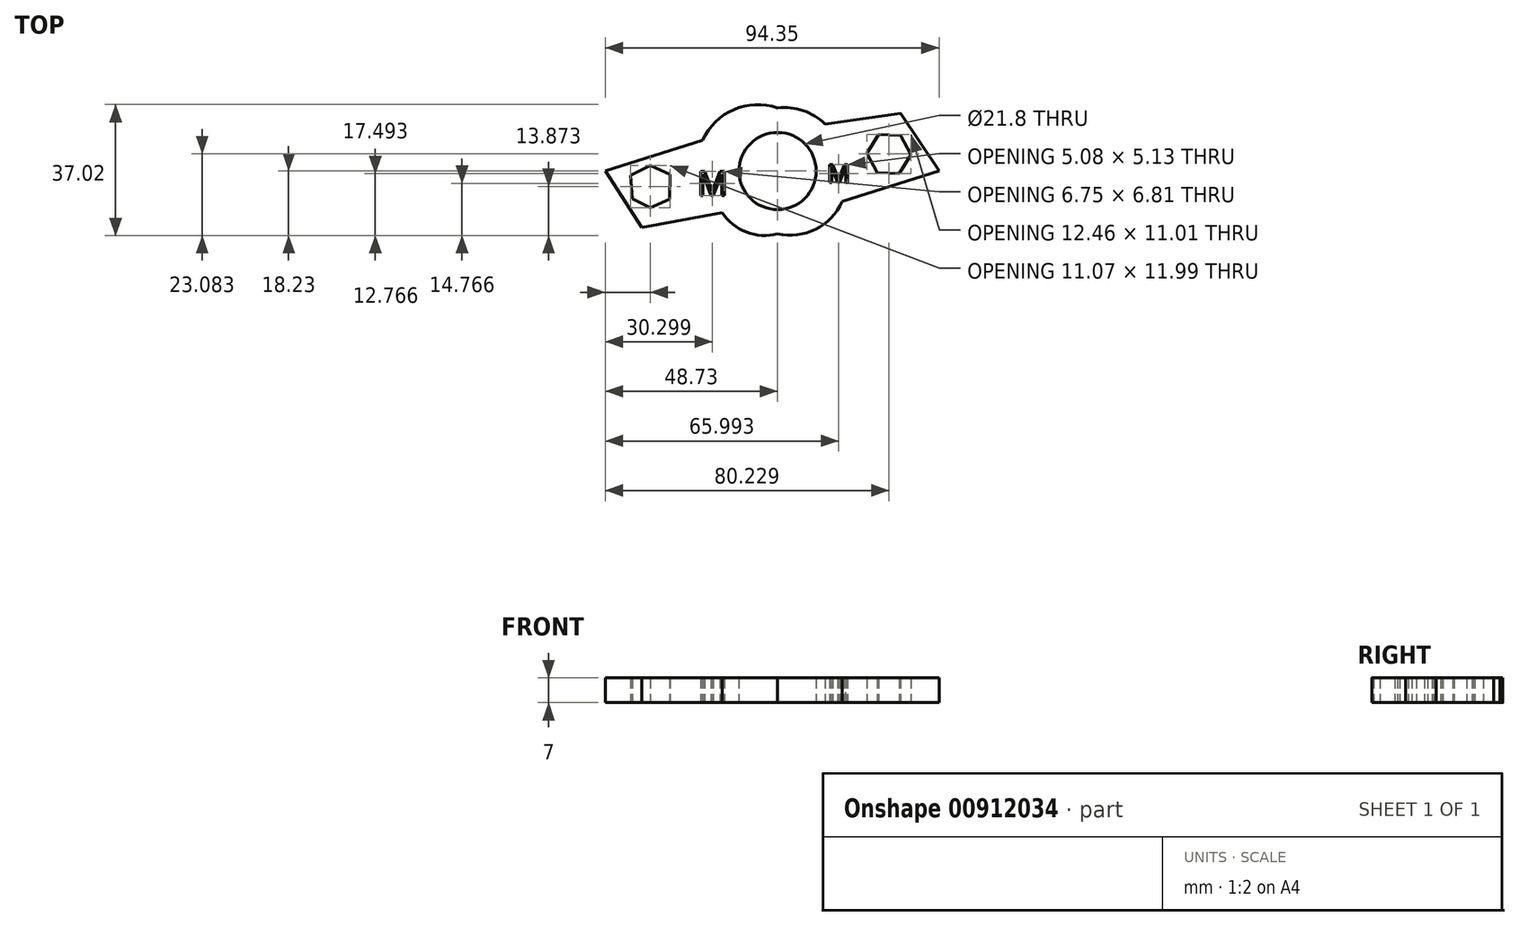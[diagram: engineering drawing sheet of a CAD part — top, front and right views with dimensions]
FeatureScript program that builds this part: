
annotation { "Feature Type Name" : "Feature", "Feature Type Description" : "" }
export const myFeature = defineFeature(function(context is Context, id is Id, definition is map)
    precondition{}
    {
        {
            var Q0;
            Q0=qCreatedBy(makeId("Top.planeOp"),FACE);
            var sketch = newSketch(context, id + "F0", { "sketchPlane" : qUnion([Q0])});
            skCircle(sketch, "E0", {"center": v(0, 0) * mm, "radius": 10.9 * mm});
            skPoint(sketch, "E1.center", {"position": v(-1.1, 0.79) * mm});
            skArc(sketch, "E2", {"start": v(0, 17.85) * mm, "mid": v(-12.4, 17.39) * mm, "end": v(-21.21, 8.67) * mm});
            skArc(sketch, "E3", {"start": v(13.42, 13.28) * mm, "mid": v(7.22, 17.07) * mm, "end": v(0, 17.85) * mm});
            skArc(sketch, "E4", {"start": v(-15.63, -11.7) * mm, "mid": v(-8.8, -17.28) * mm, "end": v(0, -17.73) * mm});
            skArc(sketch, "E5", {"start": v(0, -17.73) * mm, "mid": v(10.75, -16.43) * mm, "end": v(18.23, -8.6) * mm});
            skCircle(sketch, "E6.cCircle", {"center": v(-35.87, -4.39) * mm, "radius": 5.4 * mm, "construction": true});
            skLineSegment(sketch, "E6.0", {"start": v(-30.43, -1) * mm, "end": v(-30.52, -7.9) * mm});
            skLineSegment(sketch, "E6.1", {"start": v(-30.52, -7.9) * mm, "end": v(-35.97, -10.35) * mm});
            skLineSegment(sketch, "E6.2", {"start": v(-35.97, -10.35) * mm, "end": v(-41.05, -7.87) * mm});
            skLineSegment(sketch, "E6.3", {"start": v(-41.05, -7.87) * mm, "end": v(-41.5, -1.2) * mm});
            skLineSegment(sketch, "E6.4", {"start": v(-41.5, -1.2) * mm, "end": v(-35.96, 1.64) * mm});
            skLineSegment(sketch, "E6.5", {"start": v(-35.96, 1.64) * mm, "end": v(-30.43, -1) * mm});
            skPoint(sketch, "E6.0.midPoint", {"position": v(-30.47, -4.46) * mm});
            skLineSegment(sketch, "E7", {"start": v(-48.73, 0) * mm, "end": v(-48.73, 0) * mm});
            skLineSegment(sketch, "E8", {"start": v(-48.73, 0) * mm, "end": v(-21.21, 8.67) * mm});
            skLineSegment(sketch, "E9", {"start": v(-48.73, 0) * mm, "end": v(-38.4, -15.9) * mm});
            skLineSegment(sketch, "E10", {"start": v(-38.4, -15.9) * mm, "end": v(-15.63, -11.7) * mm});
            skLineSegment(sketch, "E11", {"start": v(18.23, -8.6) * mm, "end": v(45.62, 0) * mm});
            skLineSegment(sketch, "E12", {"start": v(45.62, 0) * mm, "end": v(34.72, 16.27) * mm});
            skLineSegment(sketch, "E13", {"start": v(34.72, 16.27) * mm, "end": v(13.42, 13.28) * mm});
            skCircle(sketch, "E14.cCircle", {"center": v(31.5, 4.85) * mm, "radius": 5.4 * mm, "construction": true});
            skLineSegment(sketch, "E14.0", {"start": v(34.8, 10.14) * mm, "end": v(37.73, 4.64) * mm});
            skLineSegment(sketch, "E14.1", {"start": v(37.73, 4.64) * mm, "end": v(34.43, -0.65) * mm});
            skLineSegment(sketch, "E14.2", {"start": v(34.43, -0.65) * mm, "end": v(28.2, -0.44) * mm});
            skLineSegment(sketch, "E14.3", {"start": v(28.2, -0.44) * mm, "end": v(25.27, 5.07) * mm});
            skLineSegment(sketch, "E14.4", {"start": v(25.27, 5.07) * mm, "end": v(28.57, 10.36) * mm});
            skLineSegment(sketch, "E14.5", {"start": v(28.57, 10.36) * mm, "end": v(34.8, 10.14) * mm});
            skPoint(sketch, "E14.0.midPoint", {"position": v(36.27, 7.4) * mm});
            skText(sketch, "E15", { "text": "M", "fontName": "OpenSans-Regular.ttf"});
            skText(sketch, "E16", { "text": "M", "fontName": "OpenSans-Regular.ttf"});
            const initialGuessF0  = {"E15": [-0.02274, -0.00687, 1, 0, 0.00687], "E16": [0.01402, -0.0033, 1, 0, 0.00517]};
            skSetInitialGuess(sketch, initialGuessF0);
            skSolve(sketch);
        }
        {
            var Q0;
            Q0=makeQuery(id+"F0.imprint","IMPRINT",FACE,{"disambiguationData":[TD([[makeQuery(id+"F0.imprint","IMPRINT",EDGE,{"derivedFrom":sQuery(id+"F0.wireOp",EDGE,"E0")}),-1.0]])]});
            extrude(context, id + "F1", {"entities" : qUnion([Q0]), "depth" : 7 * mm, "offsetDistance" : 25 * mm});
        }
    });
